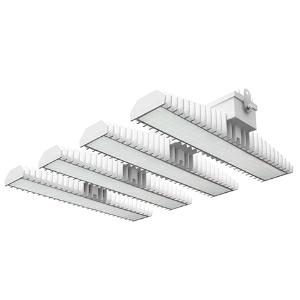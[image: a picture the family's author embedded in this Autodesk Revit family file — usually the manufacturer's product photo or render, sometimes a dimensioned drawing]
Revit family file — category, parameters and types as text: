
# Revit family: 3f_filippi_-_3f_lem_medio_3f_filippi_-_58895_a0812_-_3f_lem_4_led_200_cr_medio___vs_ef65
name_source: partatom
category: Lighting Fixtures
units: mm (PartAtom-declared; Revit-internal decimal feet)

## family parameters
Cut with Voids When Loaded = No
Host = Face
Light Source = No
Part Type = Normal
Room Calculation Point = No
Round Connector Dimension = Use Diameter
Shared = No

## types (1)
- 3F Filippi - 3F LEM Medio (1 x LED, 26931 lm, 218 W, 4000 K)
    Apparent Load = 218 VA
    Approval mark = CE
    CIE Flux Codes = 77 92 98 100 100
    Color Rendering = 80
    Color Temperature = 4000 K
    Control Gear = Electronic ballast
    Default Elevation = 1800 mm
    Description = Industrial luminaire with high light output and high luminous efficiency designed with the most innovative technologies for environments with temperature up to 55°C.

ILLUMINOTECHNICAL
Luminous efficiency 100% (DLOR 98%, ULOR 2%).
Initial luminous flux of the luminaire 26931 lm.
Medium distribution with rectangular shape.
Installation Interdistance Transv.D = 0.87 x hu - Long.D = 0.87 x hu.
Tabular UGR (CIE 117 - 4H-8H; S=0.25H; 70/50/20): RUG 21.2 - 21.2.
Beam angle: 58° - 57°.
Luminous efficacy 124 lm/W.
Lifetime (L93/B10): 30000 h. (tq+25°C)
Lifetime (L90/B10): 50000 h. (tq+25°C)
Lifetime (L85/B10): 80000 h. (tq+25°C)
Lifetime (L80/B10): 100000 h. (tq+25°C)
Lifetime (L85/B10): 50000 h. (tq+55°C)
Sudden decreased luminous flux after 50000 hours: 0% (C0).
Photobiological safety in compliance with IEC/TR 62778: RG0 risk exempt, (IEC 62471).
In compliance with IEC/EN 62722-2-1 - IEC/EN 62717 standards.

SOURCE
4 Mid-Power linear LED modules 50W/840.
Energy efficiency class (UE 2019/2020 - UE 2019/2015): C.
CIE 13.3 Colour rendering index: CRI >80 (R9 <50%).
IES TM-30 Fidelity Index: Rf = 84 Rg = 95.
CCT nominal colour temperature 4000 K.
Colour initial tolerance (MacAdam): SDCM 3.

MECHANICAL
Passive modular heatsinks in die-casted aluminium, painted in white colour.
To optimize the thermal management of the LED module, the heatsinks are oversized and provided with self-cleaning of cooling fins.
Wiring body in aluminium and galvanised steel anchored solidly to the sinks and thermally separated.
3F Lens lenses with high luminous efficiency, transparent methacrylate (PMMA), fixed to the LED modules.
Fixing brackets in stainless steel.
Luminaire with limited surface temperature. - D - (EN 60598-2-24)
Dimensions: 757x542 mm, height 133 mm. Weight 18.64 kg.
IP65 protection degree.
Mechanical strength to impacts IK06 (1 joule).
Glow-wire test resistance 650°C.

ELECTRICAL
Halogen Free electronic wiring 230V-50/60Hz, power factor 0.97, THD <25%, constant output current, class I, 2 driver.
Power of the luminaire 218 W.
ENEC - CE.
SAFE FLICKER: PstLM=<1 and SVM=<0.4 (IEC TR 61547-1 and IEC TR 63158), to ensure a more comfortable and safe light.
Luminaire compliant with EN 60598-2-22 for power supply from a centralised emergency system CPSS (Central Power Supply System), not incorporated in the luminaire - high risk areas excluded. The default power and flux are 100% in AC and 100% in DC.
Ambient temperature from -30°C to +55°C.
Temperature class T6 max 85°C.
Quick connection via M20 3P connector with 9-13 mm tightening range.
Power unit positioned on a separate compartment by the LED module to ensure optimum temperatures of cabling components, to be inspectable and maintainable.
Relative humidity UR: <85%.

INSTALLATION
Ceiling / Suspended / Wall.
All accessories dedicated to this product are available on the Catalog and on our website www.3F-Filippi.com.

ACCESSORIES
A0812 - Anti-glare microprismatic VS moulded glass, tempered, not flammable, with sealing gasket.
One required for each light module. The pack contains 10 pieces.

APPLICATIONS
In commercial environments, exhibition and industrial areas, stores, open areas.
Applications with high ambient temperature up to 55°C.
Environments in which it is necessary a total protection against falling fragments (eg environments with foodstuffs or machines with moving parts or with extreme temperature changes), use luminaires with polycarbonate lenses.

WARNING
Fixture not suitable for cold stores with an ambient temperature <0°C and/or relative humidity >85%.
Luminaire designed for disposal/recycling at end-of-life.
Replaceable (LED only) light source by a professional. Replaceable control gear by a professional.
    Height = 133 mm  [stored 0.436352 ft]
    Lamp = 1 x LED
    Lamp Light Flux = 26931 lm
    Lamp Power = 218 W
    Lamp count = 1
    Length = 757 mm
    Lifetime = 50000 h
    Luminous efficacy = 124 lm/W
    Manufacturer = 3F Filippi
    ModVariant = No
    Model = 3F Filippi - 58895+A0812 - 3F LEM 4 LED 200 CR MEDIO + VS
    Mounting Place = Ceiling
    Mounting Type = Pendant
    Number of Poles = 1
    OnlyDefault = Yes
    Power Factor = 1
    Product Name = 3F Filippi - 3F LEM Medio
    Product group = pendant luminaire
    ProductGroupID = 9
    Protection Class = Protection class I
    Protection Degree = IP 65
    RLX_Detail_Level = 1
    RLX_Emergency_Light_Flux = 0 lm
    RLX_Emergency_Type = 0
    RLX_Emergency_Type_DB = No
    RlxData = <blob elided: 120377 chars, md5=ea6cd4b3>
    Socket = socket
    Standby Power = 0 W
    System Light Flux = 26931 lm
    System Power = 218 W
    Type Comments = Product without accessories
    Type Image = 3f_filippi_-_lem_4__a0812.jpg
    URL = http://relux.com
    VarID = ---
    Voltage = 0 V
    Weight = 0.00 kg
    Width = 542 mm

note: [stored X ft] marks values corroborated as IEEE doubles in the binary element streams (Revit-internal decimal feet)

## geometry (parser evidence)
native form markers: Blend x4, Sweep x11
no freeform markers — native parametric forms only
